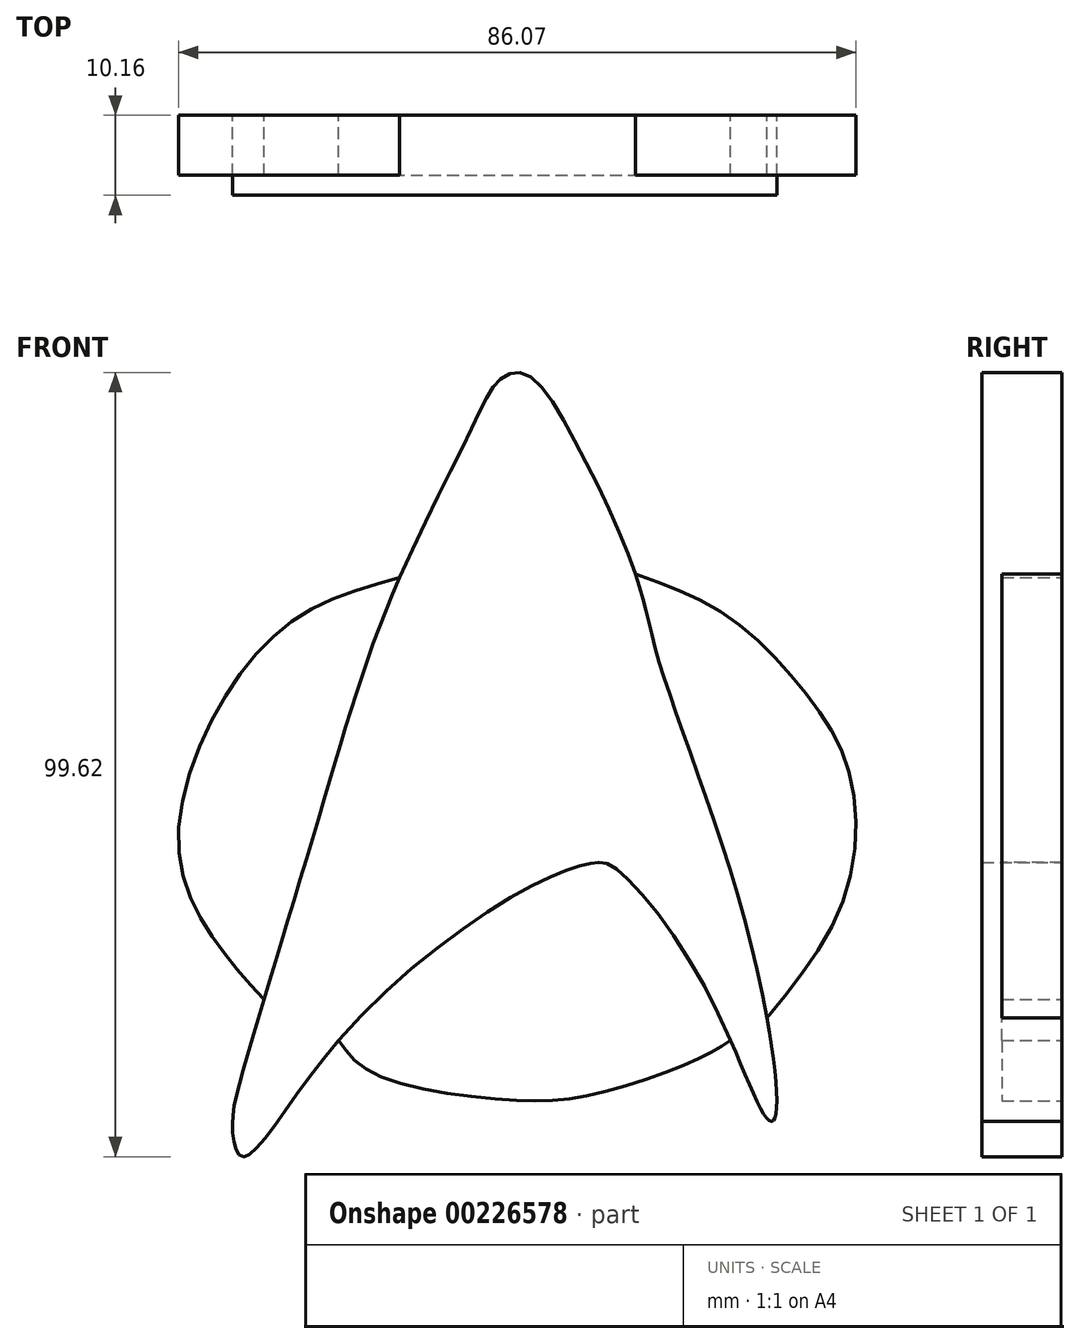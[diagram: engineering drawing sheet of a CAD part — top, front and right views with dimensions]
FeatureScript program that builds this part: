
annotation { "Feature Type Name" : "Feature", "Feature Type Description" : "" }
export const myFeature = defineFeature(function(context is Context, id is Id, definition is map)
    precondition{}
    {
        {
            var Q0;
            Q0=qCreatedBy(makeId("Front.planeOp"),FACE);
            var sketch = newSketch(context, id + "F0", { "sketchPlane" : qUnion([Q0])});
            skFitSpline(sketch, "E0", {"points": [v(12.32, 5.26) * mm, v(4.37, 22.63) * mm, v(-1.85, 30.73) * mm, v(-5.03, 29.86) * mm, v(-8.21, 24.37) * mm, v(-18.62, 2.53) * mm, v(-27.88, -25.52) * mm, v(-37.56, -57.9) * mm, v(-38.87, -65.71) * mm, v(-37.56, -68.75) * mm, v(-25.42, -54) * mm, v(0, -33.9) * mm, v(6.97, -31.44) * mm, v(9.43, -31.88) * mm, v(21.43, -47.78) * mm, v(29.23, -64.12) * mm, v(29.96, -63.98) * mm, v(26.49, -39.83) * mm, v(15.35, -6) * mm, v(12.32, 5.26) * mm]});
            skFitSpline(sketch, "E1", {"points": [v(-25.42, -54) * mm, v(-20.8, -58.27) * mm, v(-3.77, -61.54) * mm, v(6.97, -60.85) * mm, v(19.79, -56.55) * mm, v(24.39, -54) * mm], "startDerivative": vector(20.99, -29.4) * mm, "endDerivative": vector(26.46, 16.77) * mm});
            skFitSpline(sketch, "E2", {"points": [v(12.32, 5.26) * mm, v(23.91, 0) * mm, v(33.54, -9.44) * mm, v(39.39, -19.75) * mm, v(38.87, -35.75) * mm, v(29, -51.13) * mm], "startDerivative": vector(63.92, -22.63) * mm, "endDerivative": vector(-52.94, -64.63) * mm});
            skPoint(sketch, "E3.1.internal.orphan", {"position": v(-26.47, 2.53) * mm});
            skFitSpline(sketch, "E4", {"points": [v(-34.89, -48.79) * mm, v(-41.4, -40.9) * mm, v(-45.75, -29.12) * mm, v(-40.42, -11.32) * mm, v(-30.19, 0) * mm, v(-17.64, 4.83) * mm], "startDerivative": vector(-39.69, 43.14) * mm, "endDerivative": vector(67.3, 18.21) * mm});
            skSolve(sketch);
        }
        {
            var Q0;
            {var subQ1=sQuery(id+"F0.wireOp",EDGE,"E0");var subQ4=sQuery(id+"F0.wireOp",EDGE,"E3");var subQ6=makeQuery(id+"F0.imprint","INTERSECT",VERTEX,{"disambiguationData":[OD(0.0)],"derivedFrom":[subQ1,subQ4]});Q0=makeQuery(id+"F0.imprint","IMPRINT",FACE,{"disambiguationData":[TD([[makeQuery(id+"F0.imprint","IMPRINT",EDGE,{"disambiguationData":[TD([[subQ6,1.0]])],"derivedFrom":subQ1}),1.0]])]});}
            var Q1;
            {var subQ0=sQuery(id+"F0.wireOp",EDGE,"E1");var subQ1=sQuery(id+"F0.wireOp",EDGE,"E0");var subQ2=makeQuery(id+"F0.imprint","INTERSECT",VERTEX,{"disambiguationData":[OD(0.0)],"derivedFrom":[subQ1,subQ0]});Q1=makeQuery(id+"F0.imprint","IMPRINT",FACE,{"disambiguationData":[TD([[makeQuery(id+"F0.imprint","IMPRINT",EDGE,{"disambiguationData":[TD([[subQ2,1.0]])],"derivedFrom":subQ1}),1.0]])]});}
            extrude(context, id + "F1", {"entities" : qUnion([Q0, Q1]), "depth" : 10.16 * mm});
        }
        {
            var Q0;
            {var subQ0=sQuery(id+"F0.wireOp",EDGE,"E2");Q0=makeQuery(id+"F0.imprint","IMPRINT",FACE,{"disambiguationData":[TD([[makeQuery(id+"F0.imprint","IMPRINT",EDGE,{"derivedFrom":subQ0}),-1.0]])]});}
            var Q1;
            {var subQ0=sQuery(id+"F0.wireOp",EDGE,"E1");Q1=makeQuery(id+"F0.imprint","IMPRINT",FACE,{"disambiguationData":[TD([[makeQuery(id+"F0.imprint","IMPRINT",EDGE,{"derivedFrom":subQ0}),1.0]])]});}
            var Q2;
            {var subQ0=sQuery(id+"F0.wireOp",EDGE,"E4");Q2=makeQuery(id+"F0.imprint","IMPRINT",FACE,{"disambiguationData":[TD([[makeQuery(id+"F0.imprint","IMPRINT",EDGE,{"derivedFrom":subQ0}),-1.0]])]});}
            extrude(context, id + "F2", {"entities" : qUnion([Q0, Q1, Q2]), "depth" : 7.62 * mm});
        }
    });
